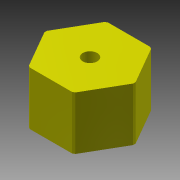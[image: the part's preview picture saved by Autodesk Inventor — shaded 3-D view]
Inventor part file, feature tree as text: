
AUTODESK INVENTOR PART (.ipt)
format: ipt  version: 2013 (Build 170138000, 138)  size: 233,472 bytes
history: native  units: mm
features: sketch x7, extrude x6, helix x1, projected_geometry x1
ambient origin geometry x8: Origin, YZ Plane, XZ Plane, XY Plane, X Axis, Y Axis, Z Axis, Center Point
bodies: Solid1 (feature_tree)
feature tree (15):
  extrude  "Extrusion1"  Depth=15.0mm TaperAngle=0.0deg
  extrude  "Extrusion2"  Depth=15.0mm TaperAngle=0.0deg
  helix  "Coil1"  [1 undecoded]
  extrude  "Extrusion8"  Depth=5.0mm TaperAngle=0.0deg
  extrude  "Extrusion9"  Depth=5.0mm
  extrude  "Extrusion10"  Depth=22.0mm
  extrude  "Extrusion11"  [1 undecoded]
  sketch  "Sketch1"  dims[d0=25.0mm d2=15.0mm d3=0.0mm]
  sketch  "Sketch2"  dims[d4=13.9mm d9=15.0mm d10=0.0mm d11=2.0mm]
  sketch  "Sketch3"  dims[d12=2.0001mm d13=10.0mm d14=100.0mm d15=0.0mm d16=90.0deg d17=90.0deg d18=0.0mm d19=0.0mm d47=5.0mm d48=0.0mm]
  sketch  "Sketch9"  dims[d49=5.0mm d50=-7.853982mm d51=5.0mm]
  sketch  "Sketch10"  dims[d53=5.0mm d54=0.0mm d55=22.0mm]
  sketch  "Sketch11"  dims[d56=0.0mm d57=0.0mm]
  sketch  "Sketch12"
  projected_geometry  "Project Cut Edges1"
note: 2 required parameter values undecoded (feature->parameter linkage not recoverable at this tier; creation-order binding heuristic only, values carry confidence <= 0.55)
